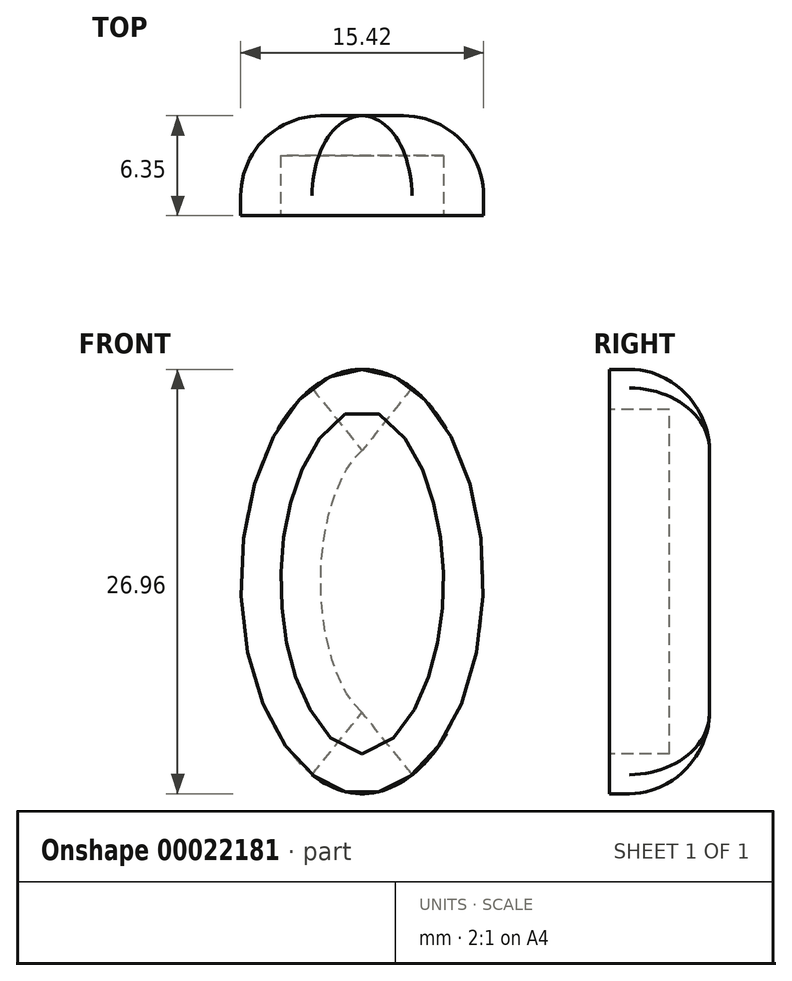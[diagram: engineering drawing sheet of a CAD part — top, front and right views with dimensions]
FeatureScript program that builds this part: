
annotation { "Feature Type Name" : "Feature", "Feature Type Description" : "" }
export const myFeature = defineFeature(function(context is Context, id is Id, definition is map)
    precondition{}
    {
        {
            var Q0;
            Q0=qCreatedBy(makeId("Front.planeOp"),FACE);
            var sketch = newSketch(context, id + "F0", { "sketchPlane" : qUnion([Q0])});
            skEllipse(sketch, "E0", {"center": v(0, 0) * mm, "majorRadius": 13.48 * mm, "minorRadius": 7.7 * mm, "majorAxis": v(0, 1)});
            skSolve(sketch);
        }
        {
            var Q0;
            Q0=makeQuery(id+"F0.imprint","IMPRINT",FACE,{"disambiguationData":[TD([[makeQuery(id+"F0.imprint","IMPRINT",EDGE,{"derivedFrom":sQuery(id+"F0.wireOp",EDGE,"E0")}),1.0]])]});
            extrude(context, id + "F1", {"entities" : qUnion([Q0]), "oppositeDirection" : true, "depth" : 6.35 * mm});
        }
        {
            var Q0;
            Q0=makeQuery(id+"F1.opExtrude","CAP_FACE",FACE,{"disambiguationData":[OSD([sQuery(id+"F0.wireOp",EDGE,"E0")])],"isStart":true});
            shell(context, id + "F2", {"entities" : qUnion([Q0]), "thickness" : 2.54 * mm});
        }
        {
            var Q0;
            Q0=makeQuery(id+"F1.opExtrude","CAP_EDGE",EDGE,{"disambiguationData":[OSD([sQuery(id+"F0.wireOp",EDGE,"E0")])],"isStart":false});
            fillet(context, id + "F3", {"entities" : qUnion([Q0]), "radius" : 5.08 * mm, "tangentPropagation" : true, "allowEdgeOverflow" : false});
        }
    });
